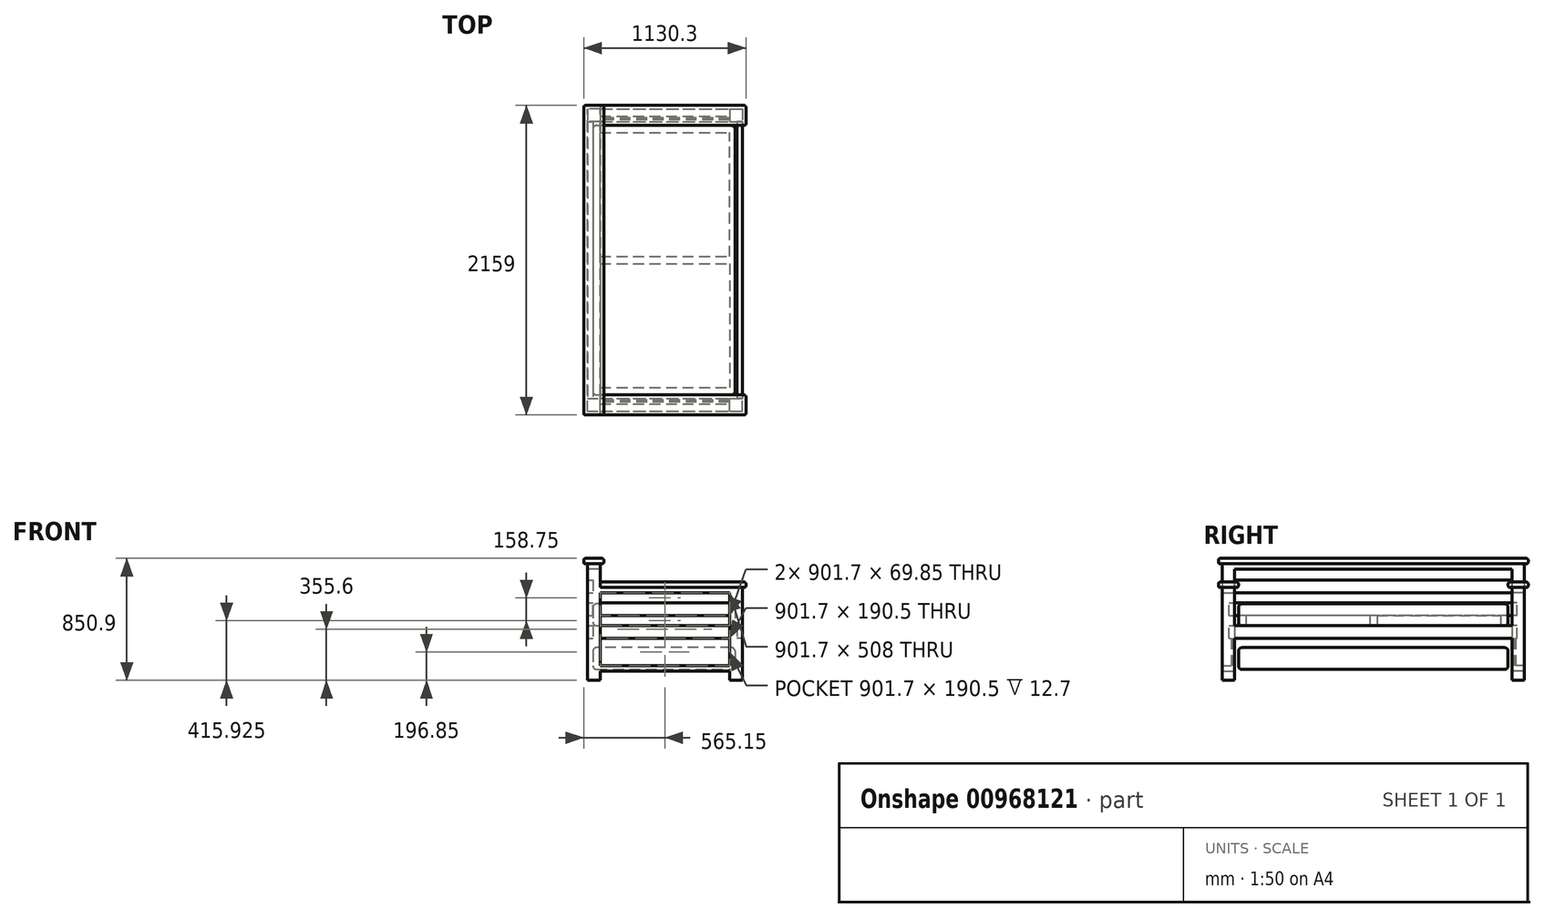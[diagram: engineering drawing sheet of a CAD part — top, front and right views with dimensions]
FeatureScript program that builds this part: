
annotation { "Feature Type Name" : "Feature", "Feature Type Description" : "" }
export const myFeature = defineFeature(function(context is Context, id is Id, definition is map)
    precondition{}
    {
        {
            var Q0;
            Q0=qCreatedBy(makeId("Front.planeOp"),FACE);
            var sketch = newSketch(context, id + "F0", { "sketchPlane" : qUnion([Q0])});
            skLineSegment(sketch, "E0.bottom", {"start": v(88.9, 647.7) * mm, "end": v(1079.5, 647.7) * mm});
            skLineSegment(sketch, "E0.left", {"start": v(88.9, 812.8) * mm, "end": v(88.9, 647.7) * mm});
            skLineSegment(sketch, "E0.right", {"start": v(1079.5, 647.7) * mm, "end": v(1079.5, 0) * mm});
            skLineSegment(sketch, "E1", {"start": v(88.9, 812.8) * mm, "end": v(0, 812.8) * mm});
            skLineSegment(sketch, "E2", {"start": v(0, 812.8) * mm, "end": v(0, 0) * mm});
            skLineSegment(sketch, "E3", {"start": v(0, 0) * mm, "end": v(88.9, 0) * mm});
            skLineSegment(sketch, "E4", {"start": v(88.9, 0) * mm, "end": v(88.9, 63.5) * mm});
            skLineSegment(sketch, "E5", {"start": v(990.6, 0) * mm, "end": v(1079.5, 0) * mm});
            skLineSegment(sketch, "E6", {"start": v(88.9, 609.6) * mm, "end": v(88.9, 101.6) * mm});
            skLineSegment(sketch, "E7", {"start": v(990.6, 101.6) * mm, "end": v(990.6, 609.6) * mm});
            skLineSegment(sketch, "E8", {"start": v(990.6, 609.6) * mm, "end": v(88.9, 609.6) * mm});
            skLineSegment(sketch, "E9", {"start": v(88.9, 101.6) * mm, "end": v(990.6, 101.6) * mm});
            skLineSegment(sketch, "E10", {"start": v(88.9, 63.5) * mm, "end": v(990.6, 63.5) * mm});
            skLineSegment(sketch, "E11.trimOffspring", {"start": v(990.6, 63.5) * mm, "end": v(990.6, 0) * mm});
            skSolve(sketch);
        }
        {
            var Q0;
            Q0=makeQuery(id+"F0.imprint","IMPRINT",FACE,{"disambiguationData":[TD([[makeQuery(id+"F0.imprint","IMPRINT",EDGE,{"derivedFrom":sQuery(id+"F0.wireOp",EDGE,"E0.bottom")}),-1.0]])]});
            extrude(context, id + "F1", {"entities" : qUnion([Q0]), "depth" : 88.9 * mm, "offsetDistance" : 25.4 * mm});
        }
        {
            var Q0;
            Q0=qCreatedBy(makeId("Front.planeOp"),FACE);
            var sketch = newSketch(context, id + "F2", { "sketchPlane" : qUnion([Q0])});
            skLineSegment(sketch, "E12.bottom", {"start": v(88.9, 292.1) * mm, "end": v(990.6, 292.1) * mm});
            skLineSegment(sketch, "E12.top", {"start": v(88.9, 381) * mm, "end": v(990.6, 381) * mm});
            skLineSegment(sketch, "E12.left", {"start": v(88.9, 292.1) * mm, "end": v(88.9, 381) * mm});
            skLineSegment(sketch, "E12.right", {"start": v(990.6, 292.1) * mm, "end": v(990.6, 381) * mm});
            skLineSegment(sketch, "E13.bottom", {"start": v(88.9, 450.85) * mm, "end": v(990.6, 450.85) * mm});
            skLineSegment(sketch, "E13.top", {"start": v(88.9, 539.75) * mm, "end": v(990.6, 539.75) * mm});
            skLineSegment(sketch, "E13.left", {"start": v(88.9, 450.85) * mm, "end": v(88.9, 539.75) * mm});
            skLineSegment(sketch, "E13.right", {"start": v(990.6, 450.85) * mm, "end": v(990.6, 539.75) * mm});
            skLineSegment(sketch, "E14", {"start": v(88.9, 381) * mm, "end": v(88.9, 450.85) * mm, "construction": true});
            skLineSegment(sketch, "E15", {"start": v(88.9, 539.75) * mm, "end": v(88.9, 609.6) * mm, "construction": true});
            skSolve(sketch);
        }
        {
            var Q0;
            Q0=makeQuery(id+"F2.imprint","IMPRINT",FACE,{"disambiguationData":[TD([[makeQuery(id+"F2.imprint","IMPRINT",EDGE,{"derivedFrom":sQuery(id+"F2.wireOp",EDGE,"E13.bottom")}),1.0]])]});
            var Q1;
            Q1=makeQuery(id+"F2.imprint","IMPRINT",FACE,{"disambiguationData":[TD([[makeQuery(id+"F2.imprint","IMPRINT",EDGE,{"derivedFrom":sQuery(id+"F2.wireOp",EDGE,"E12.bottom")}),1.0]])]});
            var Q2;
            Q2=makeQuery(id+"F2.imprint","IMPRINT",FACE,{"disambiguationData":[TD([[makeQuery(id+"F2.imprint","IMPRINT",EDGE,{"derivedFrom":sQuery(id+"F2.wireOp",EDGE,"f45WbHNY-eCAx-NiMl-likL-ScyUErPS9z3q.bottom")}),1.0]])]});
            extrude(context, id + "F3", {"entities" : qUnion([Q0, Q1, Q2]), "operationType" : NewBodyOperationType.ADD, "depth" : 38.1 * mm, "offsetDistance" : 25.4 * mm});
        }
        {
            var Q0;
            Q0=qCreatedBy(makeId("Front.planeOp"),FACE);
            var sketch = newSketch(context, id + "F4", { "sketchPlane" : qUnion([Q0])});
            skLineSegment(sketch, "E16.bottom", {"start": v(990.6, 292.1) * mm, "end": v(88.9, 292.1) * mm});
            skLineSegment(sketch, "E16.top", {"start": v(990.6, 101.6) * mm, "end": v(88.9, 101.6) * mm});
            skLineSegment(sketch, "E16.left", {"start": v(990.6, 292.1) * mm, "end": v(990.6, 101.6) * mm});
            skLineSegment(sketch, "E16.right", {"start": v(88.9, 292.1) * mm, "end": v(88.9, 101.6) * mm});
            skSolve(sketch);
        }
        {
            var Q0;
            Q0 = qSketchRegion(id + "F4", true);
            extrude(context, id + "F5", {"entities" : qUnion([Q0]), "operationType" : NewBodyOperationType.ADD, "depth" : 25.4 * mm, "offsetDistance" : 25.4 * mm, "hasSecondDirection" : true, "secondDirectionOppositeDirection" : false, "secondDirectionDepth" : 12.7 * mm});
        }
        {
            var Q0;
            Q0=qCreatedBy(makeId("Front.planeOp"),FACE);
            var sketch = newSketch(context, id + "F6", { "sketchPlane" : qUnion([Q0])});
            skLineSegment(sketch, "E17.bottom", {"start": v(88.9, 812.8) * mm, "end": v(0, 812.8) * mm});
            skLineSegment(sketch, "E17.top", {"start": v(88.9, 774.7) * mm, "end": v(0, 774.7) * mm});
            skLineSegment(sketch, "E17.left", {"start": v(88.9, 812.8) * mm, "end": v(88.9, 774.7) * mm});
            skLineSegment(sketch, "E17.right", {"start": v(0, 812.8) * mm, "end": v(0, 774.7) * mm});
            skLineSegment(sketch, "E18.bottom", {"start": v(0, 698.5) * mm, "end": v(38.1, 698.5) * mm});
            skLineSegment(sketch, "E18.top", {"start": v(0, 609.6) * mm, "end": v(38.1, 609.6) * mm});
            skLineSegment(sketch, "E18.left", {"start": v(0, 698.5) * mm, "end": v(0, 609.6) * mm});
            skLineSegment(sketch, "E18.right", {"start": v(38.1, 698.5) * mm, "end": v(38.1, 609.6) * mm});
            skLineSegment(sketch, "E19.bottom", {"start": v(0, 539.75) * mm, "end": v(38.1, 539.75) * mm});
            skLineSegment(sketch, "E19.top", {"start": v(0, 450.85) * mm, "end": v(38.1, 450.85) * mm});
            skLineSegment(sketch, "E19.left", {"start": v(0, 539.75) * mm, "end": v(0, 450.85) * mm});
            skLineSegment(sketch, "E20.bottom", {"start": v(0, 381) * mm, "end": v(38.1, 381) * mm});
            skLineSegment(sketch, "E20.top", {"start": v(0, 292.1) * mm, "end": v(38.1, 292.1) * mm});
            skLineSegment(sketch, "E20.left", {"start": v(0, 381) * mm, "end": v(0, 292.1) * mm});
            skLineSegment(sketch, "E20.right", {"start": v(38.1, 381) * mm, "end": v(38.1, 292.1) * mm});
            skLineSegment(sketch, "E21", {"start": v(38.1, 450.85) * mm, "end": v(38.1, 539.75) * mm});
            skLineSegment(sketch, "E22.bottom", {"start": v(1079.5, 381) * mm, "end": v(1041.4, 381) * mm});
            skLineSegment(sketch, "E22.top", {"start": v(1079.5, 292.1) * mm, "end": v(1041.4, 292.1) * mm});
            skLineSegment(sketch, "E22.left", {"start": v(1079.5, 381) * mm, "end": v(1079.5, 292.1) * mm});
            skLineSegment(sketch, "E22.right", {"start": v(1041.4, 381) * mm, "end": v(1041.4, 292.1) * mm});
            skSolve(sketch);
        }
        {
            var Q0;
            Q0 = qSketchRegion(id + "F6", true);
            extrude(context, id + "F7", {"entities" : qUnion([Q0]), "operationType" : NewBodyOperationType.ADD, "oppositeDirection" : true, "depth" : 965.2 * mm, "offsetDistance" : 25.4 * mm});
        }
        {
            var Q0;
            Q0=makeQuery(id+"F3.boolean.opBoolean","MERGE",FACE,{"derivedFrom":[makeQuery(id+"F1.opExtrude","CAP_FACE",FACE,{"disambiguationData":[OSD([sQuery(id+"F0.wireOp",EDGE,"E0.bottom"),sQuery(id+"F0.wireOp",EDGE,"E0.left"),sQuery(id+"F0.wireOp",EDGE,"E0.right"),sQuery(id+"F0.wireOp",EDGE,"E1"),sQuery(id+"F0.wireOp",EDGE,"E2"),sQuery(id+"F0.wireOp",EDGE,"E3"),sQuery(id+"F0.wireOp",EDGE,"E4"),sQuery(id+"F0.wireOp",EDGE,"E5"),sQuery(id+"F0.wireOp",EDGE,"E6"),sQuery(id+"F0.wireOp",EDGE,"E7"),sQuery(id+"F0.wireOp",EDGE,"E8"),sQuery(id+"F0.wireOp",EDGE,"E9"),sQuery(id+"F0.wireOp",EDGE,"E10"),sQuery(id+"F0.wireOp",EDGE,"E11.trimOffspring")])],"isStart":true}),makeQuery(id+"F3.opExtrude","CAP_FACE",FACE,{"disambiguationData":[OSD([sQuery(id+"F2.wireOp",EDGE,"f45WbHNY-eCAx-NiMl-likL-ScyUErPS9z3q.bottom"),sQuery(id+"F2.wireOp",EDGE,"f45WbHNY-eCAx-NiMl-likL-ScyUErPS9z3q.top"),sQuery(id+"F2.wireOp",EDGE,"f45WbHNY-eCAx-NiMl-likL-ScyUErPS9z3q.left"),sQuery(id+"F2.wireOp",EDGE,"f45WbHNY-eCAx-NiMl-likL-ScyUErPS9z3q.right")])],"isStart":true}),makeQuery(id+"F3.opExtrude","CAP_FACE",FACE,{"disambiguationData":[OSD([sQuery(id+"F2.wireOp",EDGE,"E12.bottom"),sQuery(id+"F2.wireOp",EDGE,"E12.top"),sQuery(id+"F2.wireOp",EDGE,"E12.left"),sQuery(id+"F2.wireOp",EDGE,"E12.right")])],"isStart":true}),makeQuery(id+"F3.opExtrude","CAP_FACE",FACE,{"disambiguationData":[OSD([sQuery(id+"F2.wireOp",EDGE,"E13.bottom"),sQuery(id+"F2.wireOp",EDGE,"E13.top"),sQuery(id+"F2.wireOp",EDGE,"E13.left"),sQuery(id+"F2.wireOp",EDGE,"E13.right")])],"isStart":true})]});
            var sketch = newSketch(context, id + "F8", { "sketchPlane" : qUnion([Q0])});
            skLineSegment(sketch, "E23.bottom", {"start": v(-965.2, 381) * mm, "end": v(-114.3, 381) * mm});
            skLineSegment(sketch, "E23.top", {"start": v(-965.2, 368.3) * mm, "end": v(-114.3, 368.3) * mm});
            skLineSegment(sketch, "E23.left", {"start": v(-965.2, 381) * mm, "end": v(-965.2, 368.3) * mm});
            skLineSegment(sketch, "E23.right", {"start": v(-114.3, 381) * mm, "end": v(-114.3, 368.3) * mm});
            skSolve(sketch);
        }
        {
            var Q0;
            Q0=makeQuery(id+"F8.imprint","IMPRINT",FACE,{"disambiguationData":[TD([[makeQuery(id+"F8.imprint","IMPRINT",EDGE,{"derivedFrom":sQuery(id+"F8.wireOp",EDGE,"E23.bottom")}),-1.0]])]});
            extrude(context, id + "F9", {"entities" : qUnion([Q0]), "operationType" : NewBodyOperationType.ADD, "depth" : 939.8 * mm, "offsetDistance" : 25.4 * mm, "hasSecondDirection" : true, "secondDirectionOppositeDirection" : false, "secondDirectionDepth" : 76.2 * mm});
        }
        {
            var Q0;
            Q0=makeQuery(id+"F7.boolean.opBoolean","MERGE",FACE,{"derivedFrom":[makeQuery(id+"F1.opExtrude","SWEPT_FACE",FACE,{"disambiguationData":[OSD([sQuery(id+"F0.wireOp",EDGE,"E0.left")])]}),makeQuery(id+"F7.opExtrude","SWEPT_FACE",FACE,{"disambiguationData":[OSD([sQuery(id+"F6.wireOp",EDGE,"E17.left")])]})]});
            var sketch = newSketch(context, id + "F10", { "sketchPlane" : qUnion([Q0])});
            skLineSegment(sketch, "E24.bottom", {"start": v(-114.3, 685.8) * mm, "end": v(25.4, 685.8) * mm});
            skLineSegment(sketch, "E24.top", {"start": v(-114.3, 647.7) * mm, "end": v(25.4, 647.7) * mm});
            skLineSegment(sketch, "E24.left", {"start": v(-114.3, 685.8) * mm, "end": v(-114.3, 647.7) * mm});
            skLineSegment(sketch, "E24.right", {"start": v(25.4, 685.8) * mm, "end": v(25.4, 647.7) * mm});
            skSolve(sketch);
        }
        {
            var Q0;
            Q0 = qSketchRegion(id + "F10", true);
            extrude(context, id + "F11", {"entities" : qUnion([Q0]), "operationType" : NewBodyOperationType.ADD, "depth" : 1016 * mm, "offsetDistance" : 25.4 * mm});
        }
        {
            var Q0;
            Q0=makeQuery(id+"F1.opExtrude","CAP_FACE",FACE,{"disambiguationData":[OSD([sQuery(id+"F0.wireOp",EDGE,"E0.bottom"),sQuery(id+"F0.wireOp",EDGE,"E0.left"),sQuery(id+"F0.wireOp",EDGE,"E0.right"),sQuery(id+"F0.wireOp",EDGE,"E1"),sQuery(id+"F0.wireOp",EDGE,"E2"),sQuery(id+"F0.wireOp",EDGE,"E3"),sQuery(id+"F0.wireOp",EDGE,"E4"),sQuery(id+"F0.wireOp",EDGE,"E5"),sQuery(id+"F0.wireOp",EDGE,"E6"),sQuery(id+"F0.wireOp",EDGE,"E7"),sQuery(id+"F0.wireOp",EDGE,"E8"),sQuery(id+"F0.wireOp",EDGE,"E9"),sQuery(id+"F0.wireOp",EDGE,"E10"),sQuery(id+"F0.wireOp",EDGE,"E11.trimOffspring")])],"isStart":false});
            var sketch = newSketch(context, id + "F12", { "sketchPlane" : qUnion([Q0])});
            skLineSegment(sketch, "E25.bottom", {"start": v(-25.4, 850.9) * mm, "end": v(114.3, 850.9) * mm});
            skLineSegment(sketch, "E25.top", {"start": v(-25.4, 812.8) * mm, "end": v(114.3, 812.8) * mm});
            skLineSegment(sketch, "E25.left", {"start": v(-25.4, 850.9) * mm, "end": v(-25.4, 812.8) * mm});
            skLineSegment(sketch, "E25.right", {"start": v(114.3, 850.9) * mm, "end": v(114.3, 812.8) * mm});
            skSolve(sketch);
        }
        {
            var Q0;
            Q0=makeQuery(id+"F12.imprint","IMPRINT",FACE,{"disambiguationData":[TD([[makeQuery(id+"F12.imprint","IMPRINT",EDGE,{"derivedFrom":sQuery(id+"F12.wireOp",EDGE,"E25.bottom")}),-1.0]])]});
            extrude(context, id + "F13", {"entities" : qUnion([Q0]), "operationType" : NewBodyOperationType.ADD, "depth" : 25.4 * mm, "offsetDistance" : 25.4 * mm, "hasSecondDirection" : true, "secondDirectionOppositeDirection" : true, "secondDirectionDepth" : 1054.1 * mm});
        }
        {
            var Q0;
            Q0=makeQuery(id+"F1.opExtrude","SWEPT_BODY",BODY,{"disambiguationData":[OSD([sQuery(id+"F0.wireOp",EDGE,"E0.bottom"),sQuery(id+"F0.wireOp",EDGE,"E0.left"),sQuery(id+"F0.wireOp",EDGE,"E0.right"),sQuery(id+"F0.wireOp",EDGE,"E1"),sQuery(id+"F0.wireOp",EDGE,"E2"),sQuery(id+"F0.wireOp",EDGE,"E3"),sQuery(id+"F0.wireOp",EDGE,"E4"),sQuery(id+"F0.wireOp",EDGE,"E5"),sQuery(id+"F0.wireOp",EDGE,"E6"),sQuery(id+"F0.wireOp",EDGE,"E7"),sQuery(id+"F0.wireOp",EDGE,"E8"),sQuery(id+"F0.wireOp",EDGE,"E9"),sQuery(id+"F0.wireOp",EDGE,"E10"),sQuery(id+"F0.wireOp",EDGE,"E11.trimOffspring")])]});
            var Q1;
            Q1=makeQuery(id+"F9.opExtrude","SWEPT_BODY",BODY,{"disambiguationData":[OSD([sQuery(id+"F8.wireOp",EDGE,"E23.bottom"),sQuery(id+"F8.wireOp",EDGE,"E23.top"),sQuery(id+"F8.wireOp",EDGE,"E23.left"),sQuery(id+"F8.wireOp",EDGE,"E23.right")])]});
            var Q2;
            Q2=makeQuery(id+"F7.opExtrude","CAP_FACE",FACE,{"disambiguationData":[OSD([sQuery(id+"F6.wireOp",EDGE,"E17.bottom"),sQuery(id+"F6.wireOp",EDGE,"E17.top"),sQuery(id+"F6.wireOp",EDGE,"E17.left"),sQuery(id+"F6.wireOp",EDGE,"E17.right")])],"isStart":false});
            mirror(context, id + "F14", {"operationType" : NewBodyOperationType.ADD, "entities" : qUnion([Q0, Q1]), "mirrorPlane" : qUnion([Q2])});
        }
        {
            var Q0;
            Q0=makeQuery(id+"F3.boolean.opBoolean","MERGE",FACE,{"derivedFrom":[makeQuery(id+"F1.opExtrude","CAP_FACE",FACE,{"disambiguationData":[OSD([sQuery(id+"F0.wireOp",EDGE,"E0.bottom"),sQuery(id+"F0.wireOp",EDGE,"E0.left"),sQuery(id+"F0.wireOp",EDGE,"E0.right"),sQuery(id+"F0.wireOp",EDGE,"E1"),sQuery(id+"F0.wireOp",EDGE,"E2"),sQuery(id+"F0.wireOp",EDGE,"E3"),sQuery(id+"F0.wireOp",EDGE,"E4"),sQuery(id+"F0.wireOp",EDGE,"E5"),sQuery(id+"F0.wireOp",EDGE,"E6"),sQuery(id+"F0.wireOp",EDGE,"E7"),sQuery(id+"F0.wireOp",EDGE,"E8"),sQuery(id+"F0.wireOp",EDGE,"E9"),sQuery(id+"F0.wireOp",EDGE,"E10"),sQuery(id+"F0.wireOp",EDGE,"E11.trimOffspring")])],"isStart":true}),makeQuery(id+"F3.opExtrude","CAP_FACE",FACE,{"disambiguationData":[OSD([sQuery(id+"F2.wireOp",EDGE,"f45WbHNY-eCAx-NiMl-likL-ScyUErPS9z3q.bottom"),sQuery(id+"F2.wireOp",EDGE,"f45WbHNY-eCAx-NiMl-likL-ScyUErPS9z3q.top"),sQuery(id+"F2.wireOp",EDGE,"f45WbHNY-eCAx-NiMl-likL-ScyUErPS9z3q.left"),sQuery(id+"F2.wireOp",EDGE,"f45WbHNY-eCAx-NiMl-likL-ScyUErPS9z3q.right")])],"isStart":true}),makeQuery(id+"F3.opExtrude","CAP_FACE",FACE,{"disambiguationData":[OSD([sQuery(id+"F2.wireOp",EDGE,"E12.bottom"),sQuery(id+"F2.wireOp",EDGE,"E12.top"),sQuery(id+"F2.wireOp",EDGE,"E12.left"),sQuery(id+"F2.wireOp",EDGE,"E12.right")])],"isStart":true}),makeQuery(id+"F3.opExtrude","CAP_FACE",FACE,{"disambiguationData":[OSD([sQuery(id+"F2.wireOp",EDGE,"E13.bottom"),sQuery(id+"F2.wireOp",EDGE,"E13.top"),sQuery(id+"F2.wireOp",EDGE,"E13.left"),sQuery(id+"F2.wireOp",EDGE,"E13.right")])],"isStart":true})]});
            var sketch = newSketch(context, id + "F15", { "sketchPlane" : qUnion([Q0])});
            skLineSegment(sketch, "E26.bottom", {"start": v(-1028.7, 533.4) * mm, "end": v(-38.1, 533.4) * mm});
            skLineSegment(sketch, "E26.top", {"start": v(-1028.7, 381) * mm, "end": v(-38.1, 381) * mm});
            skLineSegment(sketch, "E26.left", {"start": v(-1028.7, 533.4) * mm, "end": v(-1028.7, 381) * mm});
            skLineSegment(sketch, "E26.right", {"start": v(-38.1, 533.4) * mm, "end": v(-38.1, 381) * mm});
            skSolve(sketch);
        }
        {
            var Q0;
            Q0 = qSketchRegion(id + "F15", true);
            extrude(context, id + "F16", {"entities" : qUnion([Q0]), "depth" : 1905 * mm, "offsetDistance" : 25.4 * mm, "hasSecondDirection" : true, "secondDirectionOppositeDirection" : true, "secondDirectionDepth" : -25.4 * mm});
        }
        {
            var Q0;
            Q0=makeQuery(id+"F16.opExtrude","SWEPT_FACE",FACE,{"disambiguationData":[OSD([sQuery(id+"F15.wireOp",EDGE,"E26.bottom")])]});
            var Q1;
            Q1=makeQuery(id+"F16.opExtrude","SWEPT_FACE",FACE,{"disambiguationData":[OSD([sQuery(id+"F15.wireOp",EDGE,"E26.top")])]});
            var Q2;
            Q2=makeQuery(id+"F16.opExtrude","SWEPT_FACE",FACE,{"disambiguationData":[OSD([sQuery(id+"F15.wireOp",EDGE,"E26.left")])]});
            var Q3;
            Q3=makeQuery(id+"F16.opExtrude","SWEPT_FACE",FACE,{"disambiguationData":[OSD([sQuery(id+"F15.wireOp",EDGE,"E26.right")])]});
            fillet(context, id + "F17", {"entities" : qUnion([Q0, Q1, Q2, Q3]), "radius" : 25.4 * mm, "tangentPropagation" : true, "allowEdgeOverflow" : false});
        }
        {
            var Q0;
            Q0=makeQuery(id+"F16.opExtrude","SWEPT_BODY",BODY,{"disambiguationData":[OSD([sQuery(id+"F15.wireOp",EDGE,"E26.bottom"),sQuery(id+"F15.wireOp",EDGE,"E26.top"),sQuery(id+"F15.wireOp",EDGE,"E26.left"),sQuery(id+"F15.wireOp",EDGE,"E26.right")])]});
            transform(context, id + "F18", {"entities" : qUnion([Q0]), "transformType" : TransformType.TRANSLATION_3D, "dx" : 0 * mm, "dy" : 0 * mm, "dz" : -304.8 * mm, "makeCopy" : true});
        }
        {
            var Q0;
            Q0=makeQuery(id+"F13.opExtrude","CAP_FACE",FACE,{"disambiguationData":[OSD([sQuery(id+"F12.wireOp",EDGE,"E25.bottom"),sQuery(id+"F12.wireOp",EDGE,"E25.top"),sQuery(id+"F12.wireOp",EDGE,"E25.left"),sQuery(id+"F12.wireOp",EDGE,"E25.right")])],"isStart":false});
            var Q1;
            {var subQ0=makeQuery(id+"F13.opExtrude","SWEPT_FACE",FACE,{"disambiguationData":[OSD([sQuery(id+"F12.wireOp",EDGE,"E25.right")])]});Q1=makeQuery(id+"F14.boolean.opBoolean","MERGE",FACE,{"derivedFrom":[subQ0,makeQuery(id+"F14.opPattern","COPY",FACE,{"derivedFrom":subQ0,"instanceName":"1"})]});}
            var Q2;
            Q2=makeQuery(id+"F11.opExtrude","SWEPT_FACE",FACE,{"disambiguationData":[OSD([sQuery(id+"F10.wireOp",EDGE,"E24.left")])]});
            var Q3;
            Q3=makeQuery(id+"F11.opExtrude","CAP_FACE",FACE,{"disambiguationData":[OSD([sQuery(id+"F10.wireOp",EDGE,"E24.bottom"),sQuery(id+"F10.wireOp",EDGE,"E24.top"),sQuery(id+"F10.wireOp",EDGE,"E24.left"),sQuery(id+"F10.wireOp",EDGE,"E24.right")])],"isStart":false});
            var Q4;
            Q4=makeQuery(id+"F11.opExtrude","SWEPT_FACE",FACE,{"disambiguationData":[OSD([sQuery(id+"F10.wireOp",EDGE,"E24.right")])]});
            var Q5;
            Q5=makeQuery(id+"F14.opPattern","COPY",FACE,{"derivedFrom":makeQuery(id+"F11.opExtrude","SWEPT_FACE",FACE,{"disambiguationData":[OSD([sQuery(id+"F10.wireOp",EDGE,"E24.left")])]}),"instanceName":"1"});
            var Q6;
            Q6=makeQuery(id+"F14.opPattern","COPY",FACE,{"derivedFrom":makeQuery(id+"F11.opExtrude","CAP_FACE",FACE,{"disambiguationData":[OSD([sQuery(id+"F10.wireOp",EDGE,"E24.bottom"),sQuery(id+"F10.wireOp",EDGE,"E24.top"),sQuery(id+"F10.wireOp",EDGE,"E24.left"),sQuery(id+"F10.wireOp",EDGE,"E24.right")])],"isStart":false}),"instanceName":"1"});
            var Q7;
            Q7=makeQuery(id+"F14.opPattern","COPY",FACE,{"derivedFrom":makeQuery(id+"F13.opExtrude","CAP_FACE",FACE,{"disambiguationData":[OSD([sQuery(id+"F12.wireOp",EDGE,"E25.bottom"),sQuery(id+"F12.wireOp",EDGE,"E25.top"),sQuery(id+"F12.wireOp",EDGE,"E25.left"),sQuery(id+"F12.wireOp",EDGE,"E25.right")])],"isStart":false}),"instanceName":"1"});
            var Q8;
            Q8=makeQuery(id+"F14.opPattern","COPY",FACE,{"derivedFrom":makeQuery(id+"F11.opExtrude","SWEPT_FACE",FACE,{"disambiguationData":[OSD([sQuery(id+"F10.wireOp",EDGE,"E24.right")])]}),"instanceName":"1"});
            var Q9;
            {var subQ0=makeQuery(id+"F13.opExtrude","SWEPT_FACE",FACE,{"disambiguationData":[OSD([sQuery(id+"F12.wireOp",EDGE,"E25.left")])]});Q9=makeQuery(id+"F14.boolean.opBoolean","MERGE",FACE,{"derivedFrom":[subQ0,makeQuery(id+"F14.opPattern","COPY",FACE,{"derivedFrom":subQ0,"instanceName":"1"})]});}
            var Q10;
            {var subQ0=sQuery(id+"F10.wireOp",EDGE,"E24.bottom");var subQ1=makeQuery(id+"F11.opExtrude","SWEPT_FACE",FACE,{"disambiguationData":[OSD([subQ0])]});var subQ3=sQuery(id+"F10.wireOp",EDGE,"E24.left");var subQ4=makeQuery(id+"F11.opExtrude","CAP_FACE",FACE,{"disambiguationData":[OSD([subQ0,sQuery(id+"F10.wireOp",EDGE,"E24.top"),subQ3,sQuery(id+"F10.wireOp",EDGE,"E24.right")])],"isStart":true});Q10=makeQuery(id+"F11.boolean.opBoolean","SPLIT",EDGE,{"disambiguationData":[topologyDisambiguationEdgeConnected([subQ1,subQ4]),TD([makeQuery(id+"F11.opExtrude","SWEPT_FACE",FACE,{"disambiguationData":[OSD([subQ3])]})])],"derivedFrom":makeQuery(id+"F11.opExtrude","CAP_EDGE",EDGE,{"disambiguationData":[OSD([subQ0])],"isStart":true})});}
            var Q11;
            {var subQ0=sQuery(id+"F10.wireOp",EDGE,"E24.left");var subQ1=sQuery(id+"F10.wireOp",EDGE,"E24.top");Q11=makeQuery(id+"F11.boolean.opBoolean","SPLIT",EDGE,{"disambiguationData":[TD([makeQuery(id+"F11.opExtrude","SWEPT_FACE",FACE,{"disambiguationData":[OSD([subQ0])]})])],"derivedFrom":makeQuery(id+"F11.opExtrude","CAP_EDGE",EDGE,{"disambiguationData":[OSD([subQ1])],"isStart":true})});}
            var Q12;
            {var subQ0=sQuery(id+"F10.wireOp",EDGE,"E24.right");var subQ2=sQuery(id+"F10.wireOp",EDGE,"E24.bottom");var subQ3=makeQuery(id+"F11.opExtrude","SWEPT_FACE",FACE,{"disambiguationData":[OSD([subQ2])]});var subQ4=makeQuery(id+"F11.opExtrude","CAP_FACE",FACE,{"disambiguationData":[OSD([subQ2,sQuery(id+"F10.wireOp",EDGE,"E24.top"),sQuery(id+"F10.wireOp",EDGE,"E24.left"),subQ0])],"isStart":true});Q12=makeQuery(id+"F11.boolean.opBoolean","SPLIT",EDGE,{"disambiguationData":[topologyDisambiguationEdgeConnected([subQ3,subQ4]),TD([makeQuery(id+"F11.opExtrude","SWEPT_FACE",FACE,{"disambiguationData":[OSD([subQ0])]})])],"derivedFrom":makeQuery(id+"F11.opExtrude","CAP_EDGE",EDGE,{"disambiguationData":[OSD([subQ2])],"isStart":true})});}
            var Q13;
            {var subQ0=sQuery(id+"F10.wireOp",EDGE,"E24.bottom");var subQ1=makeQuery(id+"F11.opExtrude","SWEPT_FACE",FACE,{"disambiguationData":[OSD([subQ0])]});var subQ3=sQuery(id+"F10.wireOp",EDGE,"E24.left");var subQ4=makeQuery(id+"F11.opExtrude","CAP_FACE",FACE,{"disambiguationData":[OSD([subQ0,sQuery(id+"F10.wireOp",EDGE,"E24.top"),subQ3,sQuery(id+"F10.wireOp",EDGE,"E24.right")])],"isStart":true});Q13=makeQuery(id+"F14.opPattern","COPY",EDGE,{"derivedFrom":makeQuery(id+"F11.boolean.opBoolean","SPLIT",EDGE,{"disambiguationData":[topologyDisambiguationEdgeConnected([subQ1,subQ4]),TD([makeQuery(id+"F11.opExtrude","SWEPT_FACE",FACE,{"disambiguationData":[OSD([subQ3])]})])],"derivedFrom":makeQuery(id+"F11.opExtrude","CAP_EDGE",EDGE,{"disambiguationData":[OSD([subQ0])],"isStart":true})}),"instanceName":"1"});}
            var Q14;
            {var subQ0=sQuery(id+"F10.wireOp",EDGE,"E24.left");var subQ1=sQuery(id+"F10.wireOp",EDGE,"E24.top");Q14=makeQuery(id+"F14.opPattern","COPY",EDGE,{"derivedFrom":makeQuery(id+"F11.boolean.opBoolean","SPLIT",EDGE,{"disambiguationData":[TD([makeQuery(id+"F11.opExtrude","SWEPT_FACE",FACE,{"disambiguationData":[OSD([subQ0])]})])],"derivedFrom":makeQuery(id+"F11.opExtrude","CAP_EDGE",EDGE,{"disambiguationData":[OSD([subQ1])],"isStart":true})}),"instanceName":"1"});}
            var Q15;
            {var subQ0=sQuery(id+"F10.wireOp",EDGE,"E24.right");var subQ2=sQuery(id+"F10.wireOp",EDGE,"E24.bottom");var subQ3=makeQuery(id+"F11.opExtrude","SWEPT_FACE",FACE,{"disambiguationData":[OSD([subQ2])]});var subQ4=makeQuery(id+"F11.opExtrude","CAP_FACE",FACE,{"disambiguationData":[OSD([subQ2,sQuery(id+"F10.wireOp",EDGE,"E24.top"),sQuery(id+"F10.wireOp",EDGE,"E24.left"),subQ0])],"isStart":true});Q15=makeQuery(id+"F14.opPattern","COPY",EDGE,{"derivedFrom":makeQuery(id+"F11.boolean.opBoolean","SPLIT",EDGE,{"disambiguationData":[topologyDisambiguationEdgeConnected([subQ3,subQ4]),TD([makeQuery(id+"F11.opExtrude","SWEPT_FACE",FACE,{"disambiguationData":[OSD([subQ0])]})])],"derivedFrom":makeQuery(id+"F11.opExtrude","CAP_EDGE",EDGE,{"disambiguationData":[OSD([subQ2])],"isStart":true})}),"instanceName":"1"});}
            var Q16;
            {var subQ0=sQuery(id+"F10.wireOp",EDGE,"E24.right");var subQ1=sQuery(id+"F10.wireOp",EDGE,"E24.top");Q16=makeQuery(id+"F14.opPattern","COPY",EDGE,{"derivedFrom":makeQuery(id+"F11.boolean.opBoolean","SPLIT",EDGE,{"disambiguationData":[TD([makeQuery(id+"F11.opExtrude","SWEPT_FACE",FACE,{"disambiguationData":[OSD([subQ0])]})])],"derivedFrom":makeQuery(id+"F11.opExtrude","CAP_EDGE",EDGE,{"disambiguationData":[OSD([subQ1])],"isStart":true})}),"instanceName":"1"});}
            var Q17;
            {var subQ0=sQuery(id+"F10.wireOp",EDGE,"E24.right");var subQ1=sQuery(id+"F10.wireOp",EDGE,"E24.top");Q17=makeQuery(id+"F11.boolean.opBoolean","SPLIT",EDGE,{"disambiguationData":[TD([makeQuery(id+"F11.opExtrude","SWEPT_FACE",FACE,{"disambiguationData":[OSD([subQ0])]})])],"derivedFrom":makeQuery(id+"F11.opExtrude","CAP_EDGE",EDGE,{"disambiguationData":[OSD([subQ1])],"isStart":true})});}
            fillet(context, id + "F19", {"entities" : qUnion([Q0, Q1, Q2, Q3, Q4, Q5, Q6, Q7, Q8, Q9, Q10, Q11, Q12, Q13, Q14, Q15, Q16, Q17]), "radius" : 12.7 * mm, "tangentPropagation" : true, "allowEdgeOverflow" : false});
        }
    });
